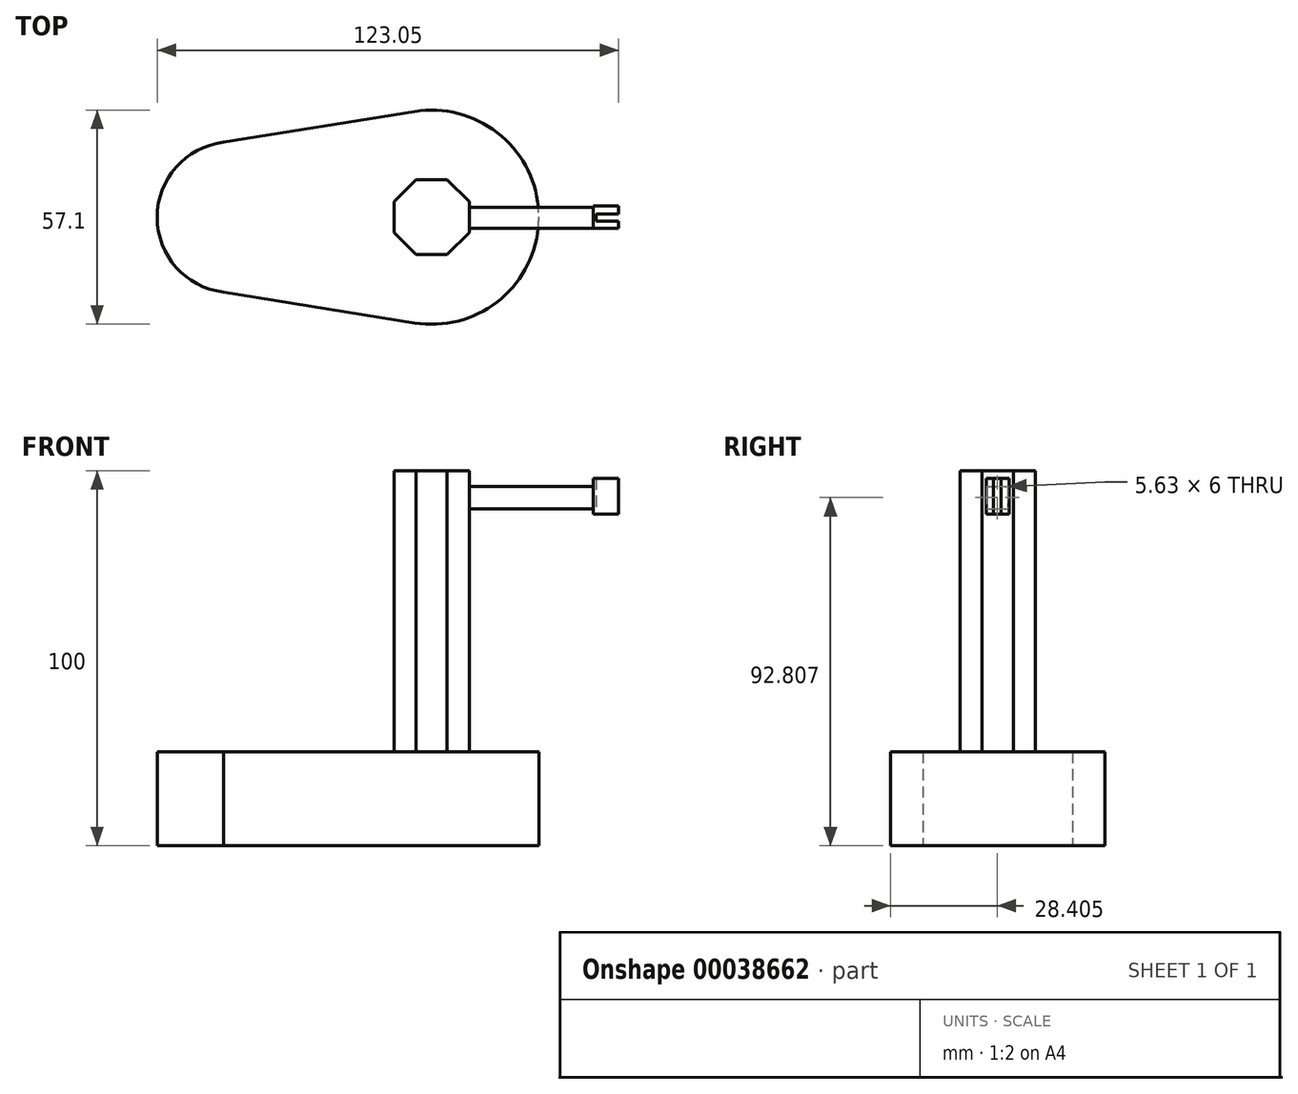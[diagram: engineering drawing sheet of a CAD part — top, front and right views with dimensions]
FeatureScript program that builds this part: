
annotation { "Feature Type Name" : "Feature", "Feature Type Description" : "" }
export const myFeature = defineFeature(function(context is Context, id is Id, definition is map)
    precondition{}
    {
        {
            var Q0;
            Q0=qCreatedBy(makeId("Top.planeOp"),FACE);
            var sketch = newSketch(context, id + "F0", { "sketchPlane" : qUnion([Q0])});
            skArc(sketch, "E0", {"start": v(-55.53, 19.98) * mm, "mid": v(-73.19, 0) * mm, "end": v(-55.53, -19.98) * mm});
            skArc(sketch, "E1", {"start": v(-4.54, -28.19) * mm, "mid": v(28.55, 0) * mm, "end": v(-4.54, 28.19) * mm});
            skLineSegment(sketch, "E2", {"start": v(-55.53, 19.98) * mm, "end": v(-4.54, 28.19) * mm});
            skLineSegment(sketch, "E3", {"start": v(-55.53, -19.98) * mm, "end": v(-4.54, -28.19) * mm});
            skSolve(sketch);
        }
        {
            var Q0;
            Q0 = qSketchRegion(id + "F0", true);
            extrude(context, id + "F1", {"entities" : qUnion([Q0]), "depth" : 25 * mm});
        }
        {
            var Q0;
            Q0=makeQuery(id+"F1.opExtrude","CAP_FACE",FACE,{"disambiguationData":[OSD([sQuery(id+"F0.wireOp",EDGE,"E0"),sQuery(id+"F0.wireOp",EDGE,"E1"),sQuery(id+"F0.wireOp",EDGE,"E2"),sQuery(id+"F0.wireOp",EDGE,"E3")])],"isStart":false});
            var sketch = newSketch(context, id + "F2", { "sketchPlane" : qUnion([Q0])});
            skCircle(sketch, "E4.cCircle", {"center": v(0, 0) * mm, "radius": 10 * mm, "construction": true});
            skLineSegment(sketch, "E4.0", {"start": v(-10, -4.14) * mm, "end": v(-10, 4.14) * mm});
            skLineSegment(sketch, "E4.1", {"start": v(-10, 4.14) * mm, "end": v(-4.14, 10) * mm});
            skLineSegment(sketch, "E4.2", {"start": v(-4.14, 10) * mm, "end": v(4.14, 10) * mm});
            skLineSegment(sketch, "E4.3", {"start": v(4.14, 10) * mm, "end": v(10, 4.14) * mm});
            skLineSegment(sketch, "E4.4", {"start": v(10, 4.14) * mm, "end": v(10, -4.14) * mm});
            skLineSegment(sketch, "E4.5", {"start": v(10, -4.14) * mm, "end": v(4.14, -10) * mm});
            skLineSegment(sketch, "E4.6", {"start": v(4.14, -10) * mm, "end": v(-4.14, -10) * mm});
            skLineSegment(sketch, "E4.7", {"start": v(-4.14, -10) * mm, "end": v(-10, -4.14) * mm});
            skPoint(sketch, "E4.0.midPoint", {"position": v(-10, 0) * mm});
            skSolve(sketch);
        }
        {
            var Q0;
            Q0 = qSketchRegion(id + "F2", true);
            extrude(context, id + "F3", {"entities" : qUnion([Q0]), "operationType" : NewBodyOperationType.ADD, "depth" : 75 * mm});
        }
        {
            var Q0;
            Q0=makeQuery(id+"F3.opExtrude","SWEPT_FACE",FACE,{"disambiguationData":[OSD([sQuery(id+"F2.wireOp",EDGE,"E4.4")])]});
            var sketch = newSketch(context, id + "F4", { "sketchPlane" : qUnion([Q0])});
            skLineSegment(sketch, "E5.bottom", {"start": v(-2.96, 95.8) * mm, "end": v(2.67, 95.8) * mm});
            skLineSegment(sketch, "E5.top", {"start": v(-2.96, 89.8) * mm, "end": v(2.67, 89.8) * mm});
            skLineSegment(sketch, "E5.left", {"start": v(-2.96, 95.8) * mm, "end": v(-2.96, 89.8) * mm});
            skLineSegment(sketch, "E5.right", {"start": v(2.67, 95.8) * mm, "end": v(2.67, 89.8) * mm});
            skSolve(sketch);
        }
        {
            var Q0;
            Q0=makeQuery(id+"F4.imprint","IMPRINT",FACE,{"disambiguationData":[TD([[makeQuery(id+"F4.imprint","IMPRINT",EDGE,{"derivedFrom":sQuery(id+"F4.wireOp",EDGE,"E5.bottom")}),-1.0]])]});
            extrude(context, id + "F5", {"entities" : qUnion([Q0]), "operationType" : NewBodyOperationType.ADD, "depth" : 35 * mm});
        }
        {
            var Q0;
            Q0=qCreatedBy(makeId("Front.planeOp"),FACE);
            var sketch = newSketch(context, id + "F6", { "sketchPlane" : qUnion([Q0])});
            skLineSegment(sketch, "E6.bottom", {"start": v(49.86, 97.89) * mm, "end": v(43.07, 97.89) * mm});
            skLineSegment(sketch, "E6.top", {"start": v(49.86, 88.33) * mm, "end": v(43.07, 88.33) * mm});
            skLineSegment(sketch, "E6.left", {"start": v(49.86, 97.89) * mm, "end": v(49.86, 88.33) * mm});
            skLineSegment(sketch, "E6.right", {"start": v(43.07, 97.89) * mm, "end": v(43.07, 88.33) * mm});
            skSolve(sketch);
        }
        {
            var Q0;
            Q0 = qSketchRegion(id + "F6", true);
            extrude(context, id + "F7", {"entities" : qUnion([Q0]), "operationType" : NewBodyOperationType.ADD, "endBound" : BoundingType.SYMMETRIC, "depth" : 6 * mm});
        }
        {
            var Q0;
            Q0=makeQuery(id+"F7.opExtrude","SWEPT_FACE",FACE,{"disambiguationData":[OSD([sQuery(id+"F6.wireOp",EDGE,"E6.left")])]});
            var sketch = newSketch(context, id + "F8", { "sketchPlane" : qUnion([Q0])});
            skLineSegment(sketch, "E7.bottom", {"start": v(-1.1, 97.89) * mm, "end": v(0.9, 97.89) * mm});
            skLineSegment(sketch, "E7.top", {"start": v(-1.1, 88.33) * mm, "end": v(0.9, 88.33) * mm});
            skLineSegment(sketch, "E7.left", {"start": v(-1.1, 97.89) * mm, "end": v(-1.1, 88.33) * mm});
            skLineSegment(sketch, "E7.right", {"start": v(0.9, 97.89) * mm, "end": v(0.9, 88.33) * mm});
            skSolve(sketch);
        }
        {
            var Q0;
            Q0 = qSketchRegion(id + "F8", true);
            extrude(context, id + "F9", {"entities" : qUnion([Q0]), "operationType" : NewBodyOperationType.REMOVE, "oppositeDirection" : true, "depth" : 6 * mm});
        }
    });
